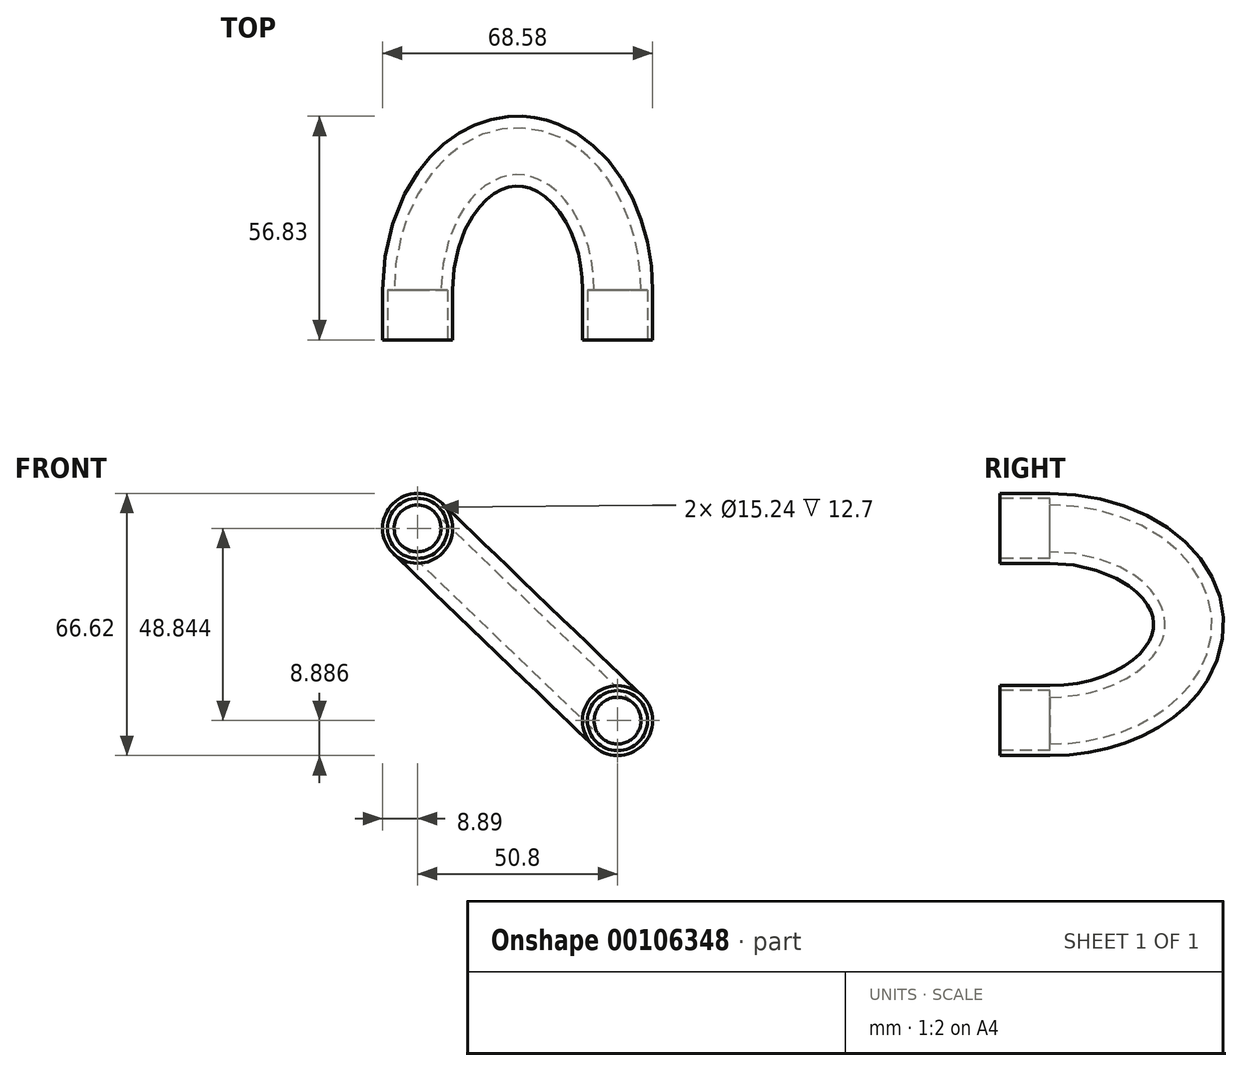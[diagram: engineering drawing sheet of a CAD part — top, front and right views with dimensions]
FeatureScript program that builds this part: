
annotation { "Feature Type Name" : "Feature", "Feature Type Description" : "" }
export const myFeature = defineFeature(function(context is Context, id is Id, definition is map)
    precondition{}
    {
        {
            var Q0;
            Q0=qCreatedBy(makeId("Top.planeOp"),FACE);
            var sketch = newSketch(context, id + "F0", { "sketchPlane" : qUnion([Q0])});
            skLineSegment(sketch, "E0", {"start": v(0, 0) * mm, "end": v(0, 12.7) * mm});
            skSolve(sketch);
        }
        {
            var Q0;
            Q0=sQuery(id+"F0.wireOp",EDGE,"E0");
            cPlane(context, id + "F1", {"entities" : qUnion([Q0]), "cplaneType" : CPlaneType.LINE_ANGLE, "offset" : 25.4 * mm, "angle" : 43.88 * degree, "width" : 152.4 * mm, "height" : 152.4 * mm});
        }
        {
            var Q0;
            Q0=qCreatedBy(id+"F1.planeOp",FACE);
            var sketch = newSketch(context, id + "F2", { "sketchPlane" : qUnion([Q0])});
            skLineSegment(sketch, "E1", {"start": v(0, 0) * mm, "end": v(0, 12.7) * mm});
            skArc(sketch, "E2", {"start": v(0, 12.7) * mm, "mid": v(35.24, 47.94) * mm, "end": v(70.47, 12.7) * mm});
            skLineSegment(sketch, "E3", {"start": v(70.47, 12.7) * mm, "end": v(70.47, 0) * mm});
            skSolve(sketch);
        }
        {
            var Q0;
            Q0=qCreatedBy(makeId("Front.planeOp"),FACE);
            var sketch = newSketch(context, id + "F3", { "sketchPlane" : qUnion([Q0])});
            skCircle(sketch, "E4", {"center": v(0, 0) * mm, "radius": 5.94 * mm});
            skCircle(sketch, "E5", {"center": v(0, 0) * mm, "radius": 8.9 * mm});
            skSolve(sketch);
        }
        {
            var Q0;
            Q0=makeQuery(id+"F3.imprint","IMPRINT",FACE,{"disambiguationData":[TD([[makeQuery(id+"F3.imprint","IMPRINT",EDGE,{"derivedFrom":sQuery(id+"F3.wireOp",EDGE,"E4")}),-1.0]])]});
            var Q1;
            Q1=sQuery(id+"F2.wireOp",EDGE,"E1");
            var Q2;
            Q2=sQuery(id+"F2.wireOp",EDGE,"E2");
            var Q3;
            Q3=sQuery(id+"F2.wireOp",EDGE,"E3");
            sweep(context, id + "F4", {"profiles" : qUnion([Q0]), "path" : qUnion([Q1, Q2, Q3])});
        }
        {
            var Q0;
            Q0=makeQuery(id+"F4.opSweep","CAP_FACE",FACE,{"disambiguationData":[OSD([sQuery(id+"F2.wireOp",VERTEX,"E1.start"),sQuery(id+"F3.wireOp",EDGE,"E4"),sQuery(id+"F3.wireOp",EDGE,"E5")])],"isStart":true});
            var sketch = newSketch(context, id + "F5", { "sketchPlane" : qUnion([Q0])});
            skCircle(sketch, "E6", {"center": v(0, 0) * mm, "radius": 7.62 * mm});
            skSolve(sketch);
        }
        {
            var Q0;
            Q0=makeQuery(id+"F4.opSweep","CAP_FACE",FACE,{"disambiguationData":[OSD([sQuery(id+"F2.wireOp",VERTEX,"E3.end"),sQuery(id+"F3.wireOp",EDGE,"E4"),sQuery(id+"F3.wireOp",EDGE,"E5")])],"isStart":false});
            var sketch = newSketch(context, id + "F6", { "sketchPlane" : qUnion([Q0])});
            skCircle(sketch, "E7", {"center": v(50.8, -48.84) * mm, "radius": 7.62 * mm});
            skSolve(sketch);
        }
        {
            var Q0;
            Q0=makeQuery(id+"F5.imprint","IMPRINT",FACE,{"disambiguationData":[TD([[makeQuery(id+"F5.imprint","IMPRINT",EDGE,{"derivedFrom":sQuery(id+"F5.wireOp",EDGE,"E6")}),1.0]])]});
            extrude(context, id + "F7", {"entities" : qUnion([Q0]), "operationType" : NewBodyOperationType.REMOVE, "oppositeDirection" : true, "depth" : 12.7 * mm});
        }
        {
            var Q0;
            Q0=makeQuery(id+"F6.imprint","IMPRINT",FACE,{"disambiguationData":[TD([[makeQuery(id+"F6.imprint","IMPRINT",EDGE,{"derivedFrom":sQuery(id+"F6.wireOp",EDGE,"E7")}),1.0]])]});
            extrude(context, id + "F8", {"entities" : qUnion([Q0]), "operationType" : NewBodyOperationType.REMOVE, "oppositeDirection" : true, "depth" : 12.7 * mm});
        }
    });
